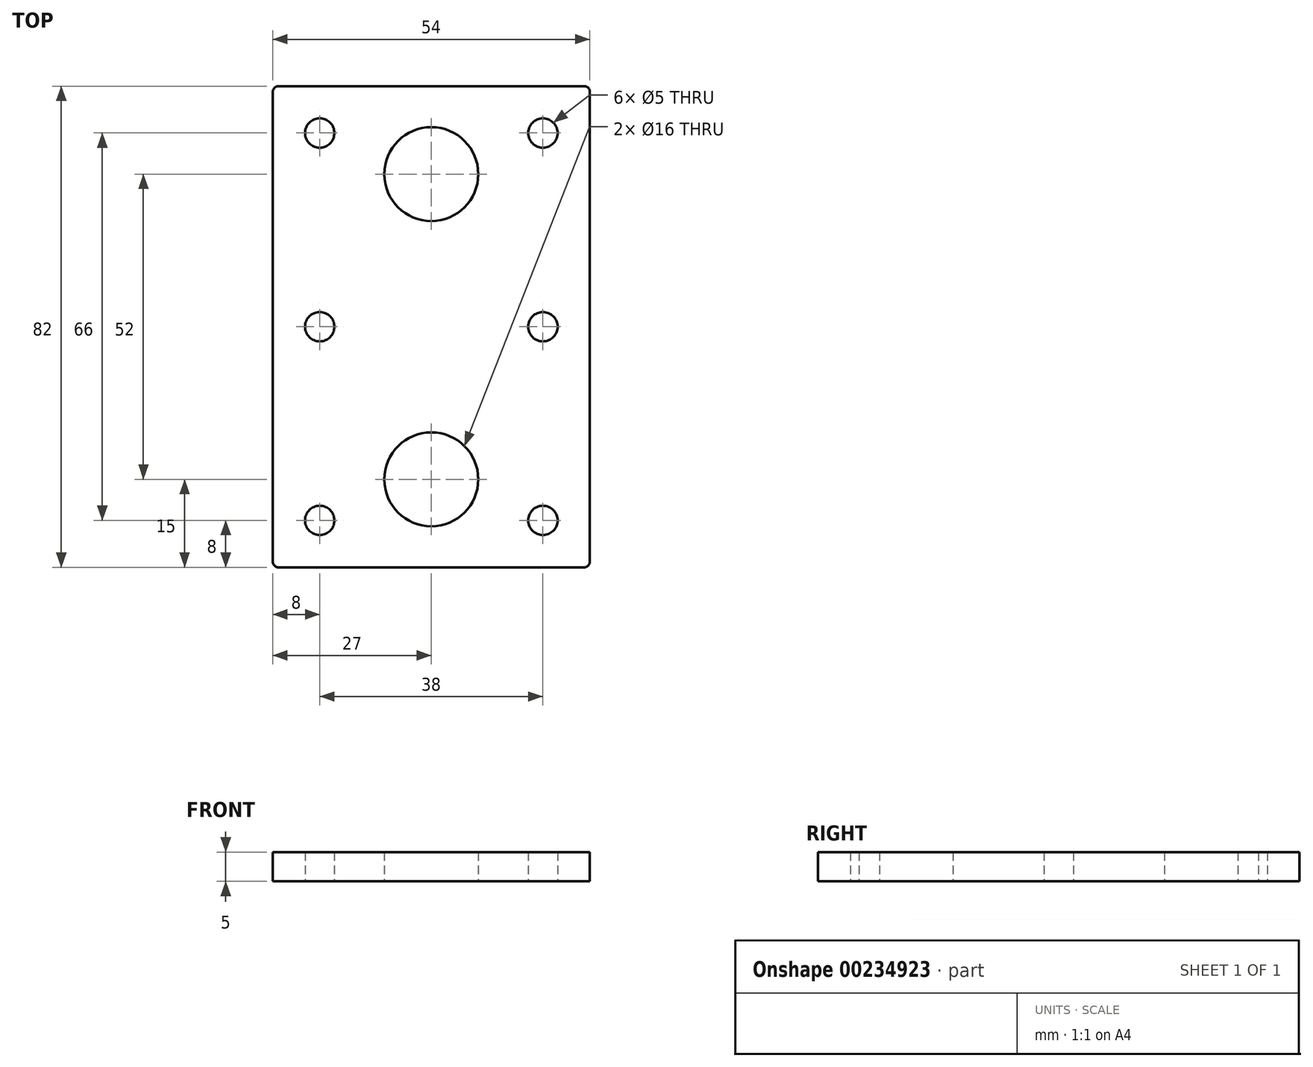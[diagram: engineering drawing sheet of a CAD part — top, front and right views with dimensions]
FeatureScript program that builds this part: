
annotation { "Feature Type Name" : "Feature", "Feature Type Description" : "" }
export const myFeature = defineFeature(function(context is Context, id is Id, definition is map)
    precondition{}
    {
        {
            var Q0;
            Q0=qCreatedBy(makeId("Top.planeOp"),FACE);
            var sketch = newSketch(context, id + "F0", { "sketchPlane" : qUnion([Q0])});
            skLineSegment(sketch, "E0.bottom", {"start": v(27, 41) * mm, "end": v(-27, 41) * mm});
            skLineSegment(sketch, "E0.top", {"start": v(27, -41) * mm, "end": v(-27, -41) * mm});
            skLineSegment(sketch, "E0.left", {"start": v(27, 41) * mm, "end": v(27, -41) * mm});
            skLineSegment(sketch, "E0.right", {"start": v(-27, 41) * mm, "end": v(-27, -41) * mm});
            skPoint(sketch, "E0.middle", {"position": v(0, 0) * mm});
            skLineSegment(sketch, "E1", {"start": v(0, -41) * mm, "end": v(0, 41) * mm, "construction": true});
            skCircle(sketch, "E2", {"center": v(0, -26) * mm, "radius": 8 * mm});
            skCircle(sketch, "E3", {"center": v(0, 26) * mm, "radius": 8 * mm});
            skLineSegment(sketch, "E4", {"start": v(-19, 41) * mm, "end": v(-19, -41) * mm, "construction": true});
            skLineSegment(sketch, "E5", {"start": v(0, 0) * mm, "end": v(-27, 0) * mm, "construction": true});
            skCircle(sketch, "E6", {"center": v(-19, 0) * mm, "radius": 2.5 * mm});
            skCircle(sketch, "E7", {"center": v(-19, -33) * mm, "radius": 2.5 * mm});
            skCircle(sketch, "E8", {"center": v(-19, 33) * mm, "radius": 2.5 * mm});
            skCircle(sketch, "E9.MirrorC", {"center": v(19, 33) * mm, "radius": 2.5 * mm});
            skCircle(sketch, "E10.MirrorC", {"center": v(19, 0) * mm, "radius": 2.5 * mm});
            skCircle(sketch, "E11.MirrorC", {"center": v(19, -33) * mm, "radius": 2.5 * mm});
            skSolve(sketch);
        }
        {
            var Q0;
            Q0 = qSketchRegion(id + "F0", true);
            extrude(context, id + "F1", {"entities" : qUnion([Q0]), "depth" : 5 * mm, "offsetDistance" : 25 * mm});
        }
        {
            var Q0;
            Q0=makeQuery(id+"F1.opExtrude","SWEPT_EDGE",EDGE,{"disambiguationData":[OSD([sQuery(id+"F0.wireOp",EDGE,"E0.top"),sQuery(id+"F0.wireOp",EDGE,"E0.left")])]});
            var Q1;
            Q1=makeQuery(id+"F1.opExtrude","SWEPT_EDGE",EDGE,{"disambiguationData":[OSD([sQuery(id+"F0.wireOp",EDGE,"E0.top"),sQuery(id+"F0.wireOp",EDGE,"E0.right")])]});
            var Q2;
            Q2=makeQuery(id+"F1.opExtrude","SWEPT_EDGE",EDGE,{"disambiguationData":[OSD([sQuery(id+"F0.wireOp",EDGE,"E0.bottom"),sQuery(id+"F0.wireOp",EDGE,"E0.right")])]});
            var Q3;
            Q3=makeQuery(id+"F1.opExtrude","SWEPT_EDGE",EDGE,{"disambiguationData":[OSD([sQuery(id+"F0.wireOp",EDGE,"E0.bottom"),sQuery(id+"F0.wireOp",EDGE,"E0.left")])]});
            fillet(context, id + "F2", {"entities" : qUnion([Q0, Q1, Q2, Q3]), "tangentPropagation" : true, "radius" : 1 * mm, "defaultsChanged" : true, "vertexSettings" : [], "allowEdgeOverflow" : false});
        }
    });
